# Revit family: DV 8000
name_source: partatom
category: Mechanical Equipment
revit_build: Autodesk Revit MEP 2013 (Build: 20120221_2030)
units: mm (PartAtom-declared; Revit-internal decimal feet)

## types (1)
- DV 8000
    Air Filters = M5 and F15
    BREEAM applicable = Yes
    Balanced supply and extract air ventilation with heat recovery = Yes
    Carbon dioxide control (optional) = Yes
    Control Optional = Co2
    Control Optional . = Humidity
    Control Optional. . = Temperature
    Control Standard = BMS/Internet
    Depth mm = 1290 mm  [stored 4.23228 ft]
    Duct Connections = 4x700x500mm
    Frequency = 50Hz
    Heat Exchanger = Cross Counterflow
    Heat Recovery = <95%\
    Height mm = 1600 mm  [stored 5.24934 ft]
    Humidity control (optional) = Yes
    Interchangeable spigot connections = Yes
    Lockable doors = Yes
    Max Air Volume  m3/hr = 9600
    Meets Building regulations Pat L2A and L2B = option
    Model = MULTI DV8000
    Part number = 9041525
    Pre Heater = option
    Safety cut off switch Pressure sensors for filter monitoring = Yes
    Summer By-pass = Yes
    Summer/Winter by-pass = Yes
    Versatile positioning ,floor and ceiling susupended options = Yes
    Voltage Supply      Single Phase = 400v ac
    Warranty = 1 Year
    Width mm = 2500 mm  [stored 8.2021 ft]

note: [stored X ft] marks values corroborated as IEEE doubles in the binary element streams (Revit-internal decimal feet)

## geometry (parser evidence)
native form markers: Sweep x1
no freeform markers — native parametric forms only
